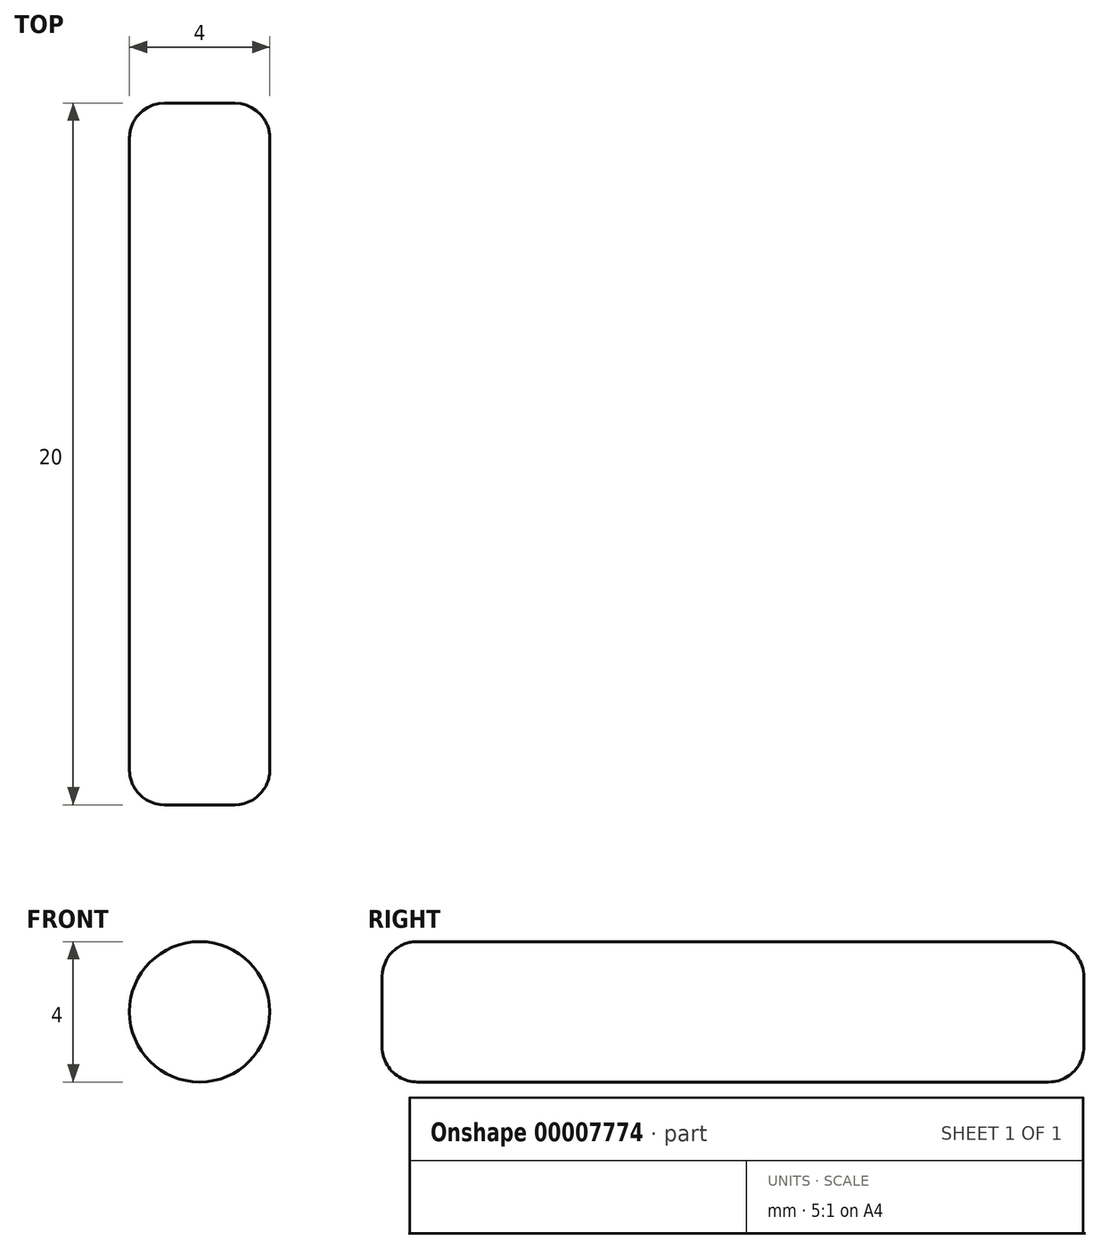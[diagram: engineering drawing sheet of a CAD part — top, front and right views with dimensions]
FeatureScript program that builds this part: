
annotation { "Feature Type Name" : "Feature", "Feature Type Description" : "" }
export const myFeature = defineFeature(function(context is Context, id is Id, definition is map)
    precondition{}
    {
        {
            var Q0;
            Q0=qCreatedBy(makeId("Front.planeOp"),FACE);
            var sketch = newSketch(context, id + "F0", { "sketchPlane" : qUnion([Q0])});
            skCircle(sketch, "E0", {"center": v(0, 0) * mm, "radius": 2 * mm});
            skSolve(sketch);
        }
        {
            var Q0;
            Q0 = qSketchRegion(id + "F0", true);
            extrude(context, id + "F1", {"entities" : qUnion([Q0]), "endBound" : BoundingType.SYMMETRIC, "depth" : 20 * mm});
        }
        {
            var Q0;
            Q0=makeQuery(id+"F1.opExtrude","CAP_EDGE",EDGE,{"disambiguationData":[OSD([sQuery(id+"F0.wireOp",EDGE,"E0")])],"isStart":false});
            var Q1;
            Q1=makeQuery(id+"F1.opExtrude","CAP_EDGE",EDGE,{"disambiguationData":[OSD([sQuery(id+"F0.wireOp",EDGE,"E0")])],"isStart":true});
            fillet(context, id + "F2", {"entities" : qUnion([Q0, Q1]), "radius" : 1 * mm, "allowEdgeOverflow" : false});
        }
    });
